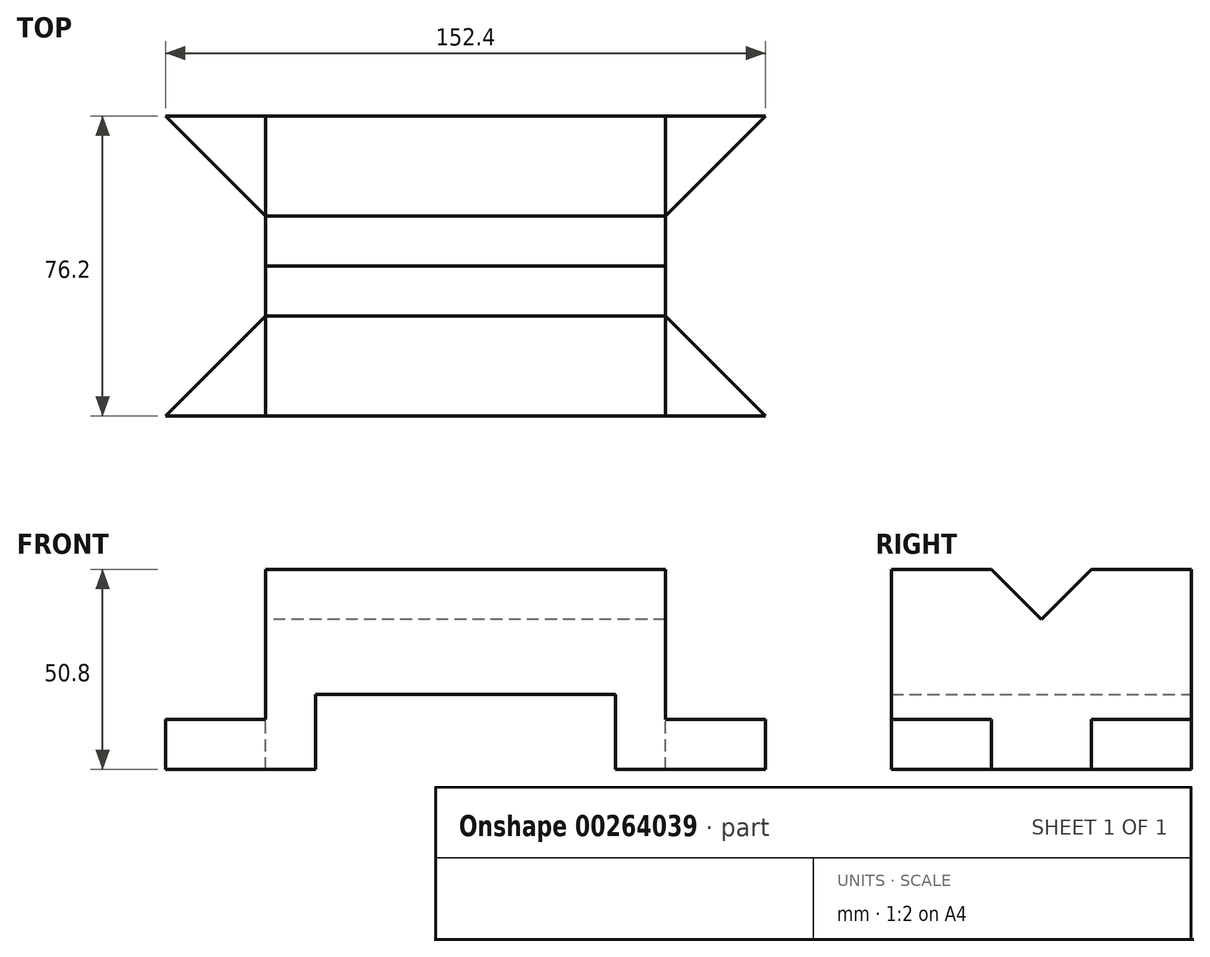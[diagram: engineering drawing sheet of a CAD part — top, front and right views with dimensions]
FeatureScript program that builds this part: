
annotation { "Feature Type Name" : "Feature", "Feature Type Description" : "" }
export const myFeature = defineFeature(function(context is Context, id is Id, definition is map)
    precondition{}
    {
        {
            var Q0;
            Q0=qCreatedBy(makeId("Front.planeOp"),FACE);
            var sketch = newSketch(context, id + "F0", { "sketchPlane" : qUnion([Q0])});
            skLineSegment(sketch, "E0", {"start": v(-76.24, -36.56) * mm, "end": v(-38.14, -36.56) * mm});
            skLineSegment(sketch, "E1", {"start": v(-38.14, -36.56) * mm, "end": v(-38.14, -17.5) * mm});
            skLineSegment(sketch, "E2", {"start": v(-38.14, -17.5) * mm, "end": v(38.06, -17.5) * mm});
            skLineSegment(sketch, "E3", {"start": v(38.06, -17.5) * mm, "end": v(38.06, -36.56) * mm});
            skLineSegment(sketch, "E4", {"start": v(38.06, -36.56) * mm, "end": v(76.16, -36.56) * mm});
            skLineSegment(sketch, "E5", {"start": v(76.16, -36.56) * mm, "end": v(76.16, -23.86) * mm});
            skLineSegment(sketch, "E6", {"start": v(76.16, -23.86) * mm, "end": v(50.76, -23.86) * mm});
            skLineSegment(sketch, "E7", {"start": v(50.76, -23.86) * mm, "end": v(50.76, 14.24) * mm});
            skLineSegment(sketch, "E8", {"start": v(50.76, 14.24) * mm, "end": v(-50.84, 14.24) * mm});
            skLineSegment(sketch, "E9", {"start": v(-50.84, 14.24) * mm, "end": v(-50.84, -23.86) * mm});
            skLineSegment(sketch, "E10", {"start": v(-50.84, -23.86) * mm, "end": v(-76.24, -23.86) * mm});
            skLineSegment(sketch, "E11", {"start": v(-76.24, -36.56) * mm, "end": v(-76.24, -23.86) * mm});
            skSolve(sketch);
        }
        {
            var Q0;
            Q0=makeQuery(id+"F0.imprint","IMPRINT",FACE,{"disambiguationData":[TD([[makeQuery(id+"F0.imprint","IMPRINT",EDGE,{"derivedFrom":sQuery(id+"F0.wireOp",EDGE,"E0")}),1.0]])]});
            extrude(context, id + "F1", {"entities" : qUnion([Q0]), "depth" : 38.1 * mm});
        }
        {
            var Q0;
            Q0=makeQuery(id+"F1.opExtrude","CAP_FACE",FACE,{"disambiguationData":[OSD([sQuery(id+"F0.wireOp",EDGE,"E0"),sQuery(id+"F0.wireOp",EDGE,"E1"),sQuery(id+"F0.wireOp",EDGE,"E2"),sQuery(id+"F0.wireOp",EDGE,"E3"),sQuery(id+"F0.wireOp",EDGE,"E4"),sQuery(id+"F0.wireOp",EDGE,"E5"),sQuery(id+"F0.wireOp",EDGE,"E6"),sQuery(id+"F0.wireOp",EDGE,"E7"),sQuery(id+"F0.wireOp",EDGE,"E8"),sQuery(id+"F0.wireOp",EDGE,"E9"),sQuery(id+"F0.wireOp",EDGE,"E10"),sQuery(id+"F0.wireOp",EDGE,"E11")])],"isStart":true});
            extrude(context, id + "F2", {"entities" : qUnion([Q0]), "operationType" : NewBodyOperationType.ADD, "depth" : 38.1 * mm});
        }
        {
            var Q0;
            {var subQ0=sQuery(id+"F0.wireOp",EDGE,"E9");Q0=makeQuery(id+"F2.boolean.opBoolean","MERGE",FACE,{"derivedFrom":[makeQuery(id+"F1.opExtrude","SWEPT_FACE",FACE,{"disambiguationData":[OSD([subQ0])]}),makeQuery(id+"F2.opExtrude","SWEPT_FACE",FACE,{"disambiguationData":[OSD([subQ0])]})]});}
            var sketch = newSketch(context, id + "F3", { "sketchPlane" : qUnion([Q0])});
            skLineSegment(sketch, "E12", {"start": v(-38.1, 14.24) * mm, "end": v(-12.7, 14.24) * mm});
            skLineSegment(sketch, "E13", {"start": v(-12.7, 14.24) * mm, "end": v(12.7, 14.24) * mm});
            skLineSegment(sketch, "E14", {"start": v(12.7, 14.24) * mm, "end": v(38.1, 14.24) * mm});
            skLineSegment(sketch, "E15", {"start": v(38.1, 14.24) * mm, "end": v(38.1, 1.54) * mm});
            skLineSegment(sketch, "E16", {"start": v(38.1, 1.54) * mm, "end": v(0, 1.54) * mm});
            skLineSegment(sketch, "E17", {"start": v(0, 1.54) * mm, "end": v(-12.7, 14.24) * mm});
            skLineSegment(sketch, "E18", {"start": v(12.7, 14.24) * mm, "end": v(0, 1.54) * mm});
            skSolve(sketch);
        }
        {
            var Q0;
            Q0=makeQuery(id+"F3.imprint","IMPRINT",FACE,{"disambiguationData":[TD([[makeQuery(id+"F3.imprint","IMPRINT",EDGE,{"derivedFrom":sQuery(id+"F3.wireOp",EDGE,"E13")}),1.0]])]});
            extrude(context, id + "F4", {"entities" : qUnion([Q0]), "operationType" : NewBodyOperationType.REMOVE, "oppositeDirection" : true, "depth" : 101.6 * mm});
        }
        {
            var Q0;
            {var subQ0=sQuery(id+"F0.wireOp",EDGE,"E10");Q0=makeQuery(id+"F2.boolean.opBoolean","MERGE",FACE,{"derivedFrom":[makeQuery(id+"F1.opExtrude","SWEPT_FACE",FACE,{"disambiguationData":[OSD([subQ0])]}),makeQuery(id+"F2.opExtrude","SWEPT_FACE",FACE,{"disambiguationData":[OSD([subQ0])]})]});}
            var sketch = newSketch(context, id + "F5", { "sketchPlane" : qUnion([Q0])});
            skLineSegment(sketch, "E19", {"start": v(-50.84, 38.1) * mm, "end": v(-50.84, 12.7) * mm});
            skLineSegment(sketch, "E20", {"start": v(-50.84, 12.7) * mm, "end": v(-76.24, 38.1) * mm});
            skLineSegment(sketch, "E21", {"start": v(-76.24, 38.1) * mm, "end": v(-50.84, 38.1) * mm});
            skLineSegment(sketch, "E22", {"start": v(-50.84, -38.1) * mm, "end": v(-50.84, -12.7) * mm});
            skLineSegment(sketch, "E23", {"start": v(-50.84, -12.7) * mm, "end": v(-76.24, -38.1) * mm});
            skLineSegment(sketch, "E24", {"start": v(-76.24, -38.1) * mm, "end": v(-50.84, -38.1) * mm});
            skSolve(sketch);
        }
        {
            var Q0;
            {var subQ0=sQuery(id+"F0.wireOp",EDGE,"E6");Q0=makeQuery(id+"F2.boolean.opBoolean","MERGE",FACE,{"derivedFrom":[makeQuery(id+"F1.opExtrude","SWEPT_FACE",FACE,{"disambiguationData":[OSD([subQ0])]}),makeQuery(id+"F2.opExtrude","SWEPT_FACE",FACE,{"disambiguationData":[OSD([subQ0])]})]});}
            var sketch = newSketch(context, id + "F6", { "sketchPlane" : qUnion([Q0])});
            skLineSegment(sketch, "E25", {"start": v(50.76, 38.1) * mm, "end": v(50.76, 12.7) * mm});
            skLineSegment(sketch, "E26", {"start": v(50.76, -38.1) * mm, "end": v(50.76, -12.7) * mm});
            skLineSegment(sketch, "E27", {"start": v(50.76, -12.7) * mm, "end": v(76.16, -38.1) * mm});
            skLineSegment(sketch, "E28", {"start": v(76.16, -38.1) * mm, "end": v(76.16, 38.1) * mm});
            skLineSegment(sketch, "E29", {"start": v(76.16, 38.1) * mm, "end": v(50.76, 12.7) * mm});
            skSolve(sketch);
        }
        {
            var Q0;
            {var subQ0=sQuery(id+"F6.wireOp",EDGE,"E27");Q0=makeQuery(id+"F6.imprint","IMPRINT",FACE,{"disambiguationData":[TD([[makeQuery(id+"F6.imprint","IMPRINT",EDGE,{"derivedFrom":subQ0}),1.0]])]});}
            var Q1;
            {var subQ0=sQuery(id+"F5.wireOp",EDGE,"E20");Q1=makeQuery(id+"F5.imprint","IMPRINT",FACE,{"disambiguationData":[TD([[makeQuery(id+"F5.imprint","IMPRINT",EDGE,{"derivedFrom":subQ0}),1.0]])]});}
            extrude(context, id + "F7", {"entities" : qUnion([Q0, Q1]), "operationType" : NewBodyOperationType.REMOVE, "oppositeDirection" : true, "depth" : 12.7 * mm});
        }
    });
